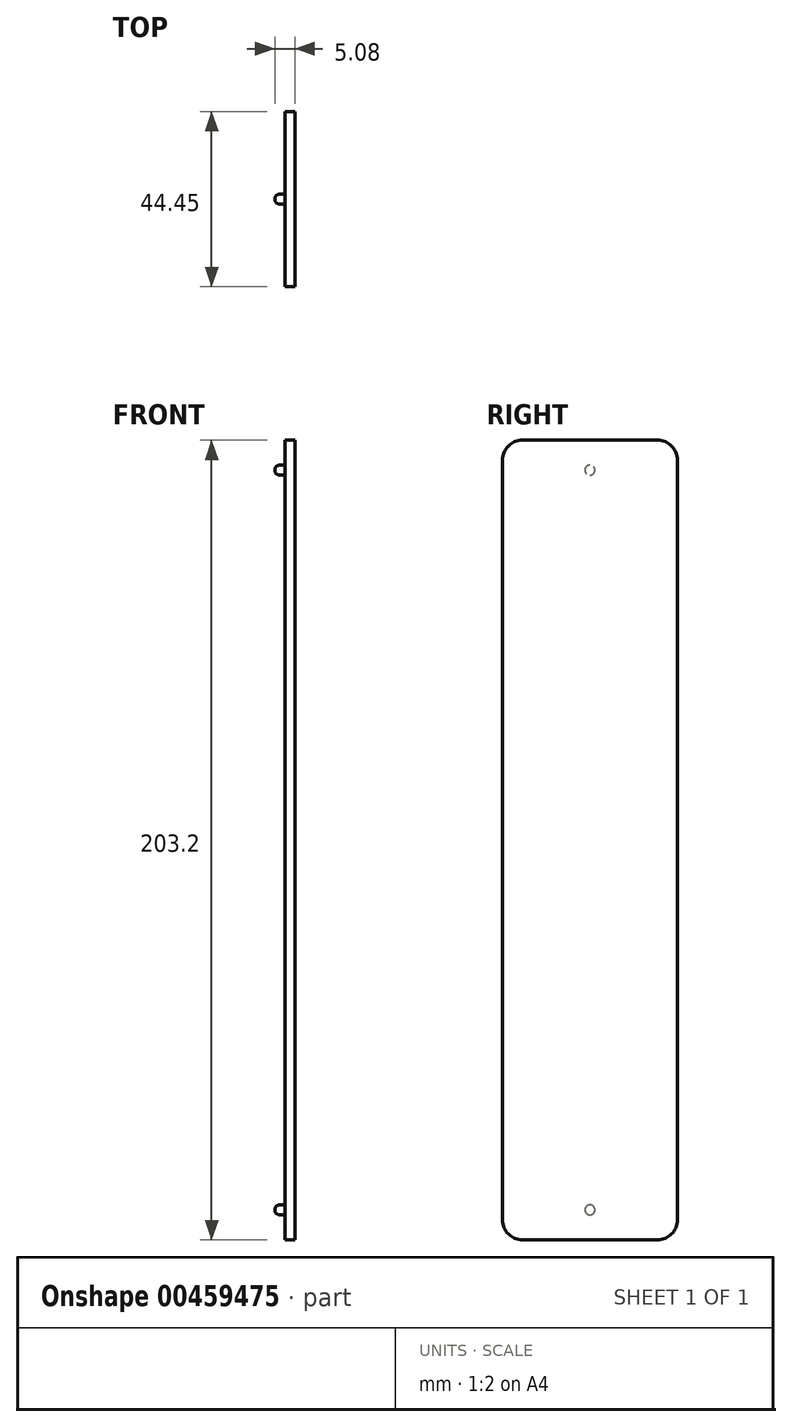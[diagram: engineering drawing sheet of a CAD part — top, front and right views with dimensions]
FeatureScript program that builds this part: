
annotation { "Feature Type Name" : "Feature", "Feature Type Description" : "" }
export const myFeature = defineFeature(function(context is Context, id is Id, definition is map)
    precondition{}
    {
        {
            var Q0;
            Q0=qCreatedBy(makeId("Right.planeOp"),FACE);
            var sketch = newSketch(context, id + "F0", { "sketchPlane" : qUnion([Q0])});
            skLineSegment(sketch, "E0", {"start": v(54.42, 102.75) * mm, "end": v(54.42, -100.45) * mm});
            skLineSegment(sketch, "E1", {"start": v(54.42, -100.45) * mm, "end": v(9.97, -100.45) * mm});
            skLineSegment(sketch, "E2", {"start": v(9.97, -100.45) * mm, "end": v(9.97, 102.75) * mm});
            skLineSegment(sketch, "E3", {"start": v(9.97, 102.75) * mm, "end": v(54.42, 102.75) * mm});
            skSolve(sketch);
        }
        {
            var Q0;
            Q0=makeQuery(id+"F0.imprint","IMPRINT",FACE,{"disambiguationData":[TD([[makeQuery(id+"F0.imprint","IMPRINT",EDGE,{"derivedFrom":sQuery(id+"F0.wireOp",EDGE,"E0")}),-1.0]])]});
            extrude(context, id + "F1", {"entities" : qUnion([Q0]), "oppositeDirection" : true, "depth" : 2.54 * mm});
        }
        {
            var Q0;
            Q0=makeQuery(id+"F1.opExtrude","SWEPT_EDGE",EDGE,{"disambiguationData":[OSD([sQuery(id+"F0.wireOp",EDGE,"E0"),sQuery(id+"F0.wireOp",EDGE,"E3")])]});
            var Q1;
            Q1=makeQuery(id+"F1.opExtrude","SWEPT_EDGE",EDGE,{"disambiguationData":[OSD([sQuery(id+"F0.wireOp",EDGE,"E2"),sQuery(id+"F0.wireOp",EDGE,"E3")])]});
            var Q2;
            Q2=makeQuery(id+"F1.opExtrude","SWEPT_EDGE",EDGE,{"disambiguationData":[OSD([sQuery(id+"F0.wireOp",EDGE,"E0"),sQuery(id+"F0.wireOp",EDGE,"E1")])]});
            var Q3;
            Q3=makeQuery(id+"F1.opExtrude","SWEPT_EDGE",EDGE,{"disambiguationData":[OSD([sQuery(id+"F0.wireOp",EDGE,"E1"),sQuery(id+"F0.wireOp",EDGE,"E2")])]});
            fillet(context, id + "F2", {"entities" : qUnion([Q0, Q1, Q2, Q3]), "radius" : 5.08 * mm, "tangentPropagation" : true, "allowEdgeOverflow" : false});
        }
        {
            var Q0;
            Q0=makeQuery(id+"F1.opExtrude","CAP_FACE",FACE,{"disambiguationData":[OSD([sQuery(id+"F0.wireOp",EDGE,"E0"),sQuery(id+"F0.wireOp",EDGE,"E1"),sQuery(id+"F0.wireOp",EDGE,"E2"),sQuery(id+"F0.wireOp",EDGE,"E3")])],"isStart":false});
            var sketch = newSketch(context, id + "F3", { "sketchPlane" : qUnion([Q0])});
            skCircle(sketch, "E4", {"center": v(-32.2, 95.13) * mm, "radius": 1.27 * mm});
            skPoint(sketch, "E4.centerSnap0", {"position": v(-32.2, 102.75) * mm});
            skSolve(sketch);
        }
        {
            var Q0;
            Q0=makeQuery(id+"F3.imprint","IMPRINT",FACE,{"disambiguationData":[TD([[makeQuery(id+"F3.imprint","IMPRINT",EDGE,{"derivedFrom":sQuery(id+"F3.wireOp",EDGE,"E4")}),1.0]])]});
            extrude(context, id + "F4", {"entities" : qUnion([Q0]), "operationType" : NewBodyOperationType.ADD, "depth" : 2.54 * mm});
        }
        {
            var Q0;
            Q0=makeQuery(id+"F4.opExtrude","CAP_EDGE",EDGE,{"disambiguationData":[OSD([sQuery(id+"F3.wireOp",EDGE,"E4")])],"isStart":false});
            fillet(context, id + "F5", {"entities" : qUnion([Q0]), "radius" : 1.27 * mm, "tangentPropagation" : true, "allowEdgeOverflow" : false});
        }
        {
            var Q0;
            Q0=makeQuery(id+"F1.opExtrude","CAP_FACE",FACE,{"disambiguationData":[OSD([sQuery(id+"F0.wireOp",EDGE,"E0"),sQuery(id+"F0.wireOp",EDGE,"E1"),sQuery(id+"F0.wireOp",EDGE,"E2"),sQuery(id+"F0.wireOp",EDGE,"E3")])],"isStart":false});
            var sketch = newSketch(context, id + "F6", { "sketchPlane" : qUnion([Q0])});
            skCircle(sketch, "E5", {"center": v(-32.2, -92.83) * mm, "radius": 1.27 * mm});
            skPoint(sketch, "E5.centerSnap0", {"position": v(-32.2, -100.45) * mm});
            skSolve(sketch);
        }
        {
            var Q0;
            Q0=makeQuery(id+"F6.imprint","IMPRINT",FACE,{"disambiguationData":[TD([[makeQuery(id+"F6.imprint","IMPRINT",EDGE,{"derivedFrom":sQuery(id+"F6.wireOp",EDGE,"E5")}),1.0]])]});
            extrude(context, id + "F7", {"entities" : qUnion([Q0]), "operationType" : NewBodyOperationType.ADD, "depth" : 2.54 * mm});
        }
        {
            var Q0;
            Q0=makeQuery(id+"F7.opExtrude","CAP_EDGE",EDGE,{"disambiguationData":[OSD([sQuery(id+"F6.wireOp",EDGE,"E5")])],"isStart":false});
            fillet(context, id + "F8", {"entities" : qUnion([Q0]), "radius" : 1.27 * mm, "tangentPropagation" : true, "allowEdgeOverflow" : false});
        }
    });
